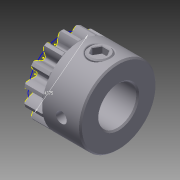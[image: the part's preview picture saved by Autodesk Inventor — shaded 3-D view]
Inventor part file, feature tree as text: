
AUTODESK INVENTOR PART (.ipt)
format: ipt  version: 2012 (Build 160160000, 160)  size: 762,368 bytes
history: native  units: in
note: dims shown in document units (in); Inventor stores cm internally (conversion verified against a paired STEP export)
features: other x4, sketch x1
ambient origin geometry x8: Origin, YZ Plane, XZ Plane, XY Plane, X Axis, Y Axis, Z Axis, Center Point
bodies: Solid1 (feature_tree), Solid2 (feature_tree)
feature tree (5):
  other  "s1066z-032s014-2.ipt"
  other  "79602::s1066z-032s014-2.ipt"
  other  "79602_1::s1066z-032s014-2.ipt"
  sketch  "Sketch1"  dims[d0=0.3937in]
  other  "TaggingFeature1"
